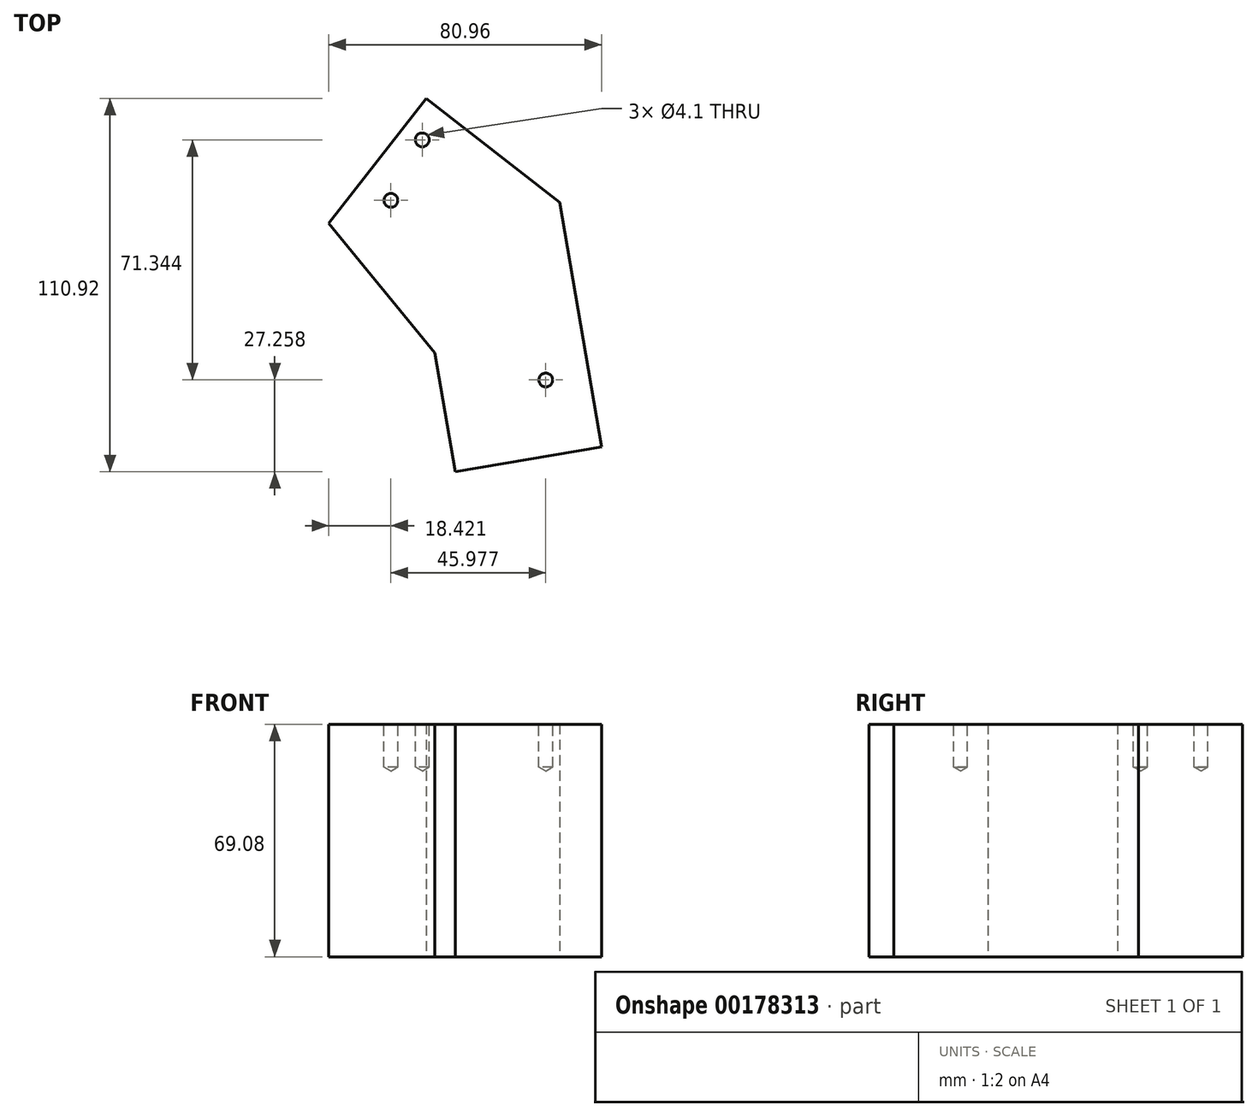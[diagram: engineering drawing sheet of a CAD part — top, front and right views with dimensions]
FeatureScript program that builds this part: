
annotation { "Feature Type Name" : "Feature", "Feature Type Description" : "" }
export const myFeature = defineFeature(function(context is Context, id is Id, definition is map)
    precondition{}
    {
        {
            var Q0;
            Q0=qCreatedBy(makeId("Top.planeOp"),FACE);
            var sketch = newSketch(context, id + "F0", { "sketchPlane" : qUnion([Q0])});
            skLineSegment(sketch, "E0", {"start": v(-42.76, 23.35) * mm, "end": v(-13.89, 60.48) * mm});
            skLineSegment(sketch, "E1", {"start": v(-13.89, 60.48) * mm, "end": v(25.81, 29.62) * mm});
            skLineSegment(sketch, "E2", {"start": v(25.81, 29.62) * mm, "end": v(38.2, -43.03) * mm});
            skLineSegment(sketch, "E3", {"start": v(38.2, -43.03) * mm, "end": v(-5.24, -50.44) * mm});
            skLineSegment(sketch, "E4", {"start": v(-5.24, -50.44) * mm, "end": v(-11.27, -15.1) * mm});
            skLineSegment(sketch, "E5", {"start": v(-11.27, -15.1) * mm, "end": v(-42.76, 23.35) * mm});
            skSolve(sketch);
        }
        {
            var Q0;
            Q0 = qSketchRegion(id + "F0", true);
            extrude(context, id + "F1", {"entities" : qUnion([Q0]), "endBound" : BoundingType.SYMMETRIC, "depth" : 69.1 * mm});
        }
        {
            var Q0;
            Q0=makeQuery(id+"F1.opExtrude","CAP_FACE",FACE,{"disambiguationData":[OSD([sQuery(id+"F0.wireOp",EDGE,"E0"),sQuery(id+"F0.wireOp",EDGE,"E1"),sQuery(id+"F0.wireOp",EDGE,"E2"),sQuery(id+"F0.wireOp",EDGE,"E3"),sQuery(id+"F0.wireOp",EDGE,"E4"),sQuery(id+"F0.wireOp",EDGE,"E5")])],"isStart":false});
            var sketch = newSketch(context, id + "F2", { "sketchPlane" : qUnion([Q0])});
            skPoint(sketch, "E6", {"position": v(-15.02, 48.16) * mm});
            skPoint(sketch, "E7", {"position": v(-24.34, 30.2) * mm});
            skPoint(sketch, "E8", {"position": v(21.64, -23.18) * mm});
            skSolve(sketch);
        }
        {
            var Q0;
            Q0=sQuery(id+"F2.wireOp",VERTEX,"E6");
            var Q1;
            Q1=sQuery(id+"F2.wireOp",VERTEX,"E7");
            var Q2;
            Q2=sQuery(id+"F2.wireOp",VERTEX,"E8");
            var Q3;
            Q3=makeQuery(id+"F1.opExtrude","SWEPT_BODY",BODY,{"disambiguationData":[OSD([sQuery(id+"F0.wireOp",EDGE,"E0"),sQuery(id+"F0.wireOp",EDGE,"E1"),sQuery(id+"F0.wireOp",EDGE,"E2"),sQuery(id+"F0.wireOp",EDGE,"E3"),sQuery(id+"F0.wireOp",EDGE,"E4"),sQuery(id+"F0.wireOp",EDGE,"E5")])]});
            hole(context, id + "F3", {"style" : HoleStyle.SIMPLE, "endStyle" : HoleEndStyle.BLIND, "standardTappedOrClearance" : lookupTablePath({ "standard" : "ISO", "engagement" : "75%", "pitch" : "0.9 mm", "size" : "M5", "type" : "Tapped" }), "standardBlindInLast" : lookupTablePath({ "standard" : "ISO", "engagement" : "75%", "pitch" : "0.9 mm", "size" : "M5", "type" : "Tapped" }), "holeDiameter" : 4.1 * mm, "holeDepth" : 12.7 * mm, "locations" : qUnion([Q0, Q1, Q2]), "scope" : qUnion([Q3])});
        }
    });
